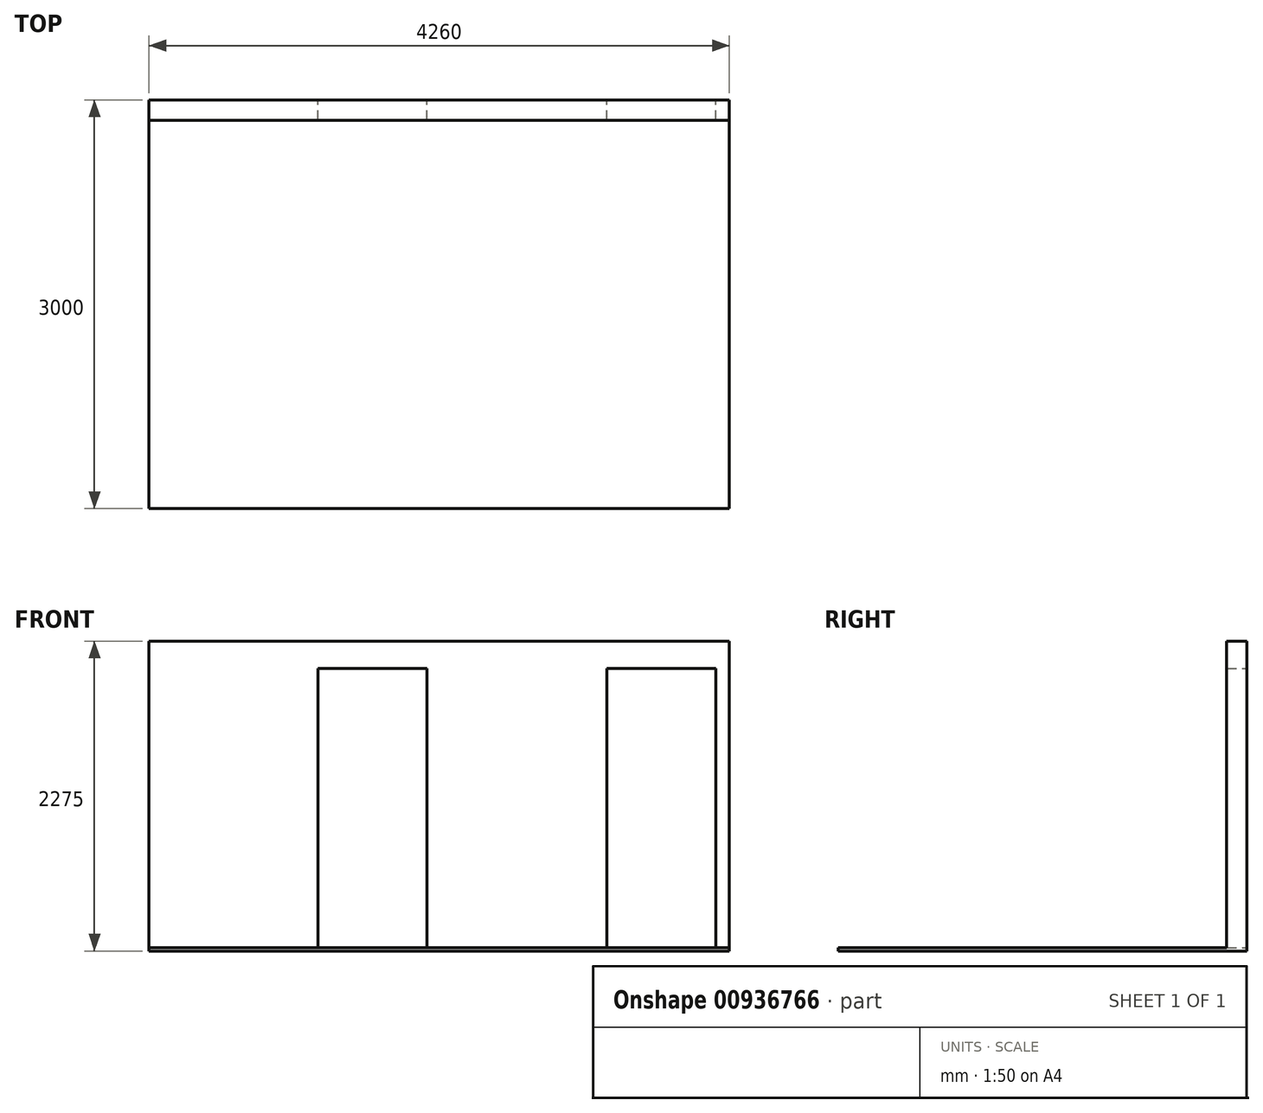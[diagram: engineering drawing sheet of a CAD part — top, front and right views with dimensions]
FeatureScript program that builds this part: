
annotation { "Feature Type Name" : "Feature", "Feature Type Description" : "" }
export const myFeature = defineFeature(function(context is Context, id is Id, definition is map)
    precondition{}
    {
        {
            var Q0;
            Q0=qCreatedBy(makeId("Front.planeOp"),FACE);
            var sketch = newSketch(context, id + "F0", { "sketchPlane" : qUnion([Q0])});
            skLineSegment(sketch, "E0.bottom", {"start": v(-2551.85, 1244.92) * mm, "end": v(1708.15, 1244.92) * mm});
            skLineSegment(sketch, "E0.left", {"start": v(-2551.85, 1244.92) * mm, "end": v(-2551.85, -1005.08) * mm});
            skLineSegment(sketch, "E0.right", {"start": v(1708.15, 1244.92) * mm, "end": v(1708.15, -1005.08) * mm});
            skLineSegment(sketch, "E1", {"start": v(-2551.85, -1005.08) * mm, "end": v(-1311.85, -1005.08) * mm});
            skLineSegment(sketch, "E2", {"start": v(-1311.85, -1005.08) * mm, "end": v(-1311.85, 1044.92) * mm});
            skLineSegment(sketch, "E3", {"start": v(-1311.85, 1044.92) * mm, "end": v(-511.85, 1044.92) * mm});
            skLineSegment(sketch, "E4", {"start": v(-511.85, 1044.92) * mm, "end": v(-511.85, -1005.08) * mm});
            skLineSegment(sketch, "E5", {"start": v(-511.85, -1005.08) * mm, "end": v(808.15, -1005.08) * mm});
            skLineSegment(sketch, "E6", {"start": v(808.15, -1005.08) * mm, "end": v(808.15, 1044.92) * mm});
            skLineSegment(sketch, "E7", {"start": v(808.15, 1044.92) * mm, "end": v(1608.15, 1044.92) * mm});
            skLineSegment(sketch, "E8", {"start": v(1608.15, 1044.92) * mm, "end": v(1608.15, -1005.08) * mm});
            skLineSegment(sketch, "E9", {"start": v(1608.15, -1005.08) * mm, "end": v(1708.15, -1005.08) * mm});
            skSolve(sketch);
        }
        {
            var Q0;
            Q0 = qSketchRegion(id + "F0", true);
            extrude(context, id + "F1", {"entities" : qUnion([Q0]), "depth" : 150 * mm, "offsetDistance" : 25 * mm});
        }
        {
            var Q0;
            Q0=makeQuery(id+"F1.opExtrude","SWEPT_FACE",FACE,{"disambiguationData":[OSD([sQuery(id+"F0.wireOp",EDGE,"E1")])]});
            var sketch = newSketch(context, id + "F2", { "sketchPlane" : qUnion([Q0])});
            skLineSegment(sketch, "E10.bottom", {"start": v(-2551.85, 0) * mm, "end": v(1708.15, 0) * mm});
            skLineSegment(sketch, "E10.top", {"start": v(-2551.85, 3000) * mm, "end": v(1708.15, 3000) * mm});
            skLineSegment(sketch, "E10.left", {"start": v(-2551.85, 0) * mm, "end": v(-2551.85, 3000) * mm});
            skLineSegment(sketch, "E10.right", {"start": v(1708.15, 0) * mm, "end": v(1708.15, 3000) * mm});
            skSolve(sketch);
        }
        {
            var Q0;
            Q0 = qSketchRegion(id + "F2", true);
            extrude(context, id + "F3", {"entities" : qUnion([Q0]), "operationType" : NewBodyOperationType.ADD, "depth" : 25 * mm, "offsetDistance" : 25 * mm});
        }
    });
